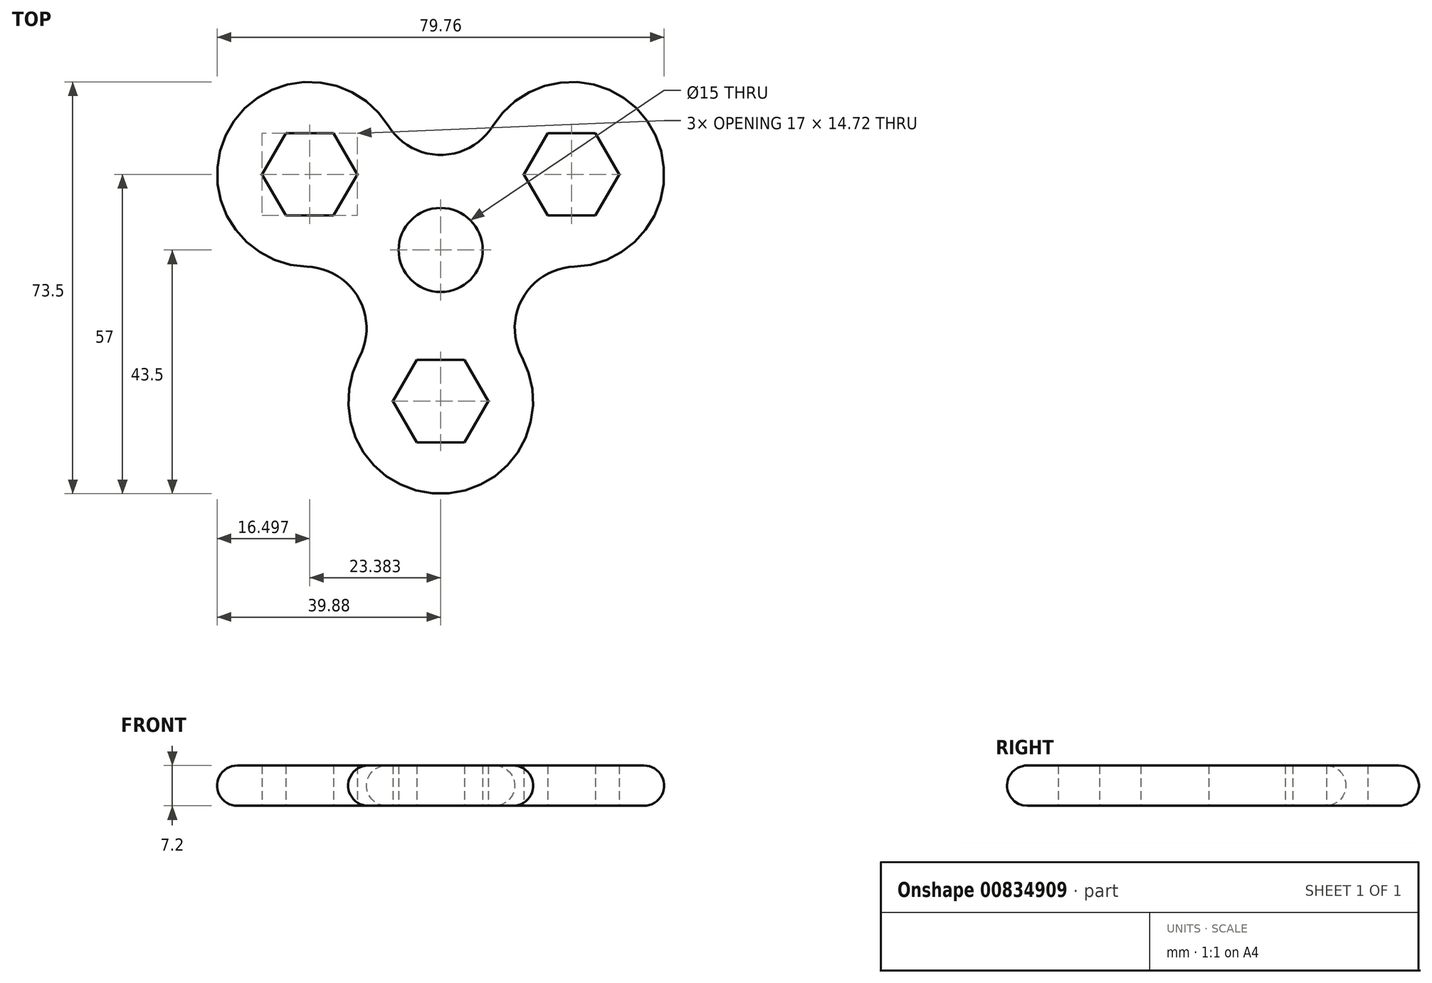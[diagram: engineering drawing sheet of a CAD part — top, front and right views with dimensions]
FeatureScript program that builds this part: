
annotation { "Feature Type Name" : "Feature", "Feature Type Description" : "" }
export const myFeature = defineFeature(function(context is Context, id is Id, definition is map)
    precondition{}
    {
        {
            var Q0;
            Q0=qCreatedBy(makeId("Top.planeOp"),FACE);
            var sketch = newSketch(context, id + "F0", { "sketchPlane" : qUnion([Q0])});
            skLineSegment(sketch, "E0", {"start": v(0, 0) * mm, "end": v(0, -27) * mm, "construction": true});
            skArc(sketch, "E1", {"start": v(-14.54, -19.2) * mm, "mid": v(0, -43.5) * mm, "end": v(14.54, -19.2) * mm});
            skLineSegment(sketch, "E2", {"start": v(-34.97, -27) * mm, "end": v(30.88, -27) * mm, "construction": true});
            skArc(sketch, "E3", {"start": v(23.89, -3) * mm, "mid": v(14.7, -8.49) * mm, "end": v(14.54, -19.2) * mm});
            skArc(sketch, "E4.1.0", {"start": v(-9.35, 22.18) * mm, "mid": v(-37.67, 21.75) * mm, "end": v(-23.89, -3) * mm});
            skArc(sketch, "E4.1.1", {"start": v(-14.54, -19.2) * mm, "mid": v(-14.7, -8.49) * mm, "end": v(-23.89, -3) * mm});
            skArc(sketch, "E4.2.0", {"start": v(23.89, -3) * mm, "mid": v(37.67, 21.75) * mm, "end": v(9.35, 22.18) * mm});
            skArc(sketch, "E4.2.1", {"start": v(-9.35, 22.18) * mm, "mid": v(0, 16.97) * mm, "end": v(9.35, 22.18) * mm});
            skPoint(sketch, "E4.center", {"position": v(0, 0) * mm});
            skLineSegment(sketch, "E4.anchor2", {"start": v(0, 0) * mm, "end": v(23.38, 13.5) * mm, "construction": true});
            skCircle(sketch, "E5", {"center": v(0, 0) * mm, "radius": 7.5 * mm});
            skCircle(sketch, "E6.cCircle", {"center": v(0, -27) * mm, "radius": 7.36 * mm, "construction": true});
            skLineSegment(sketch, "E6.0", {"start": v(4.25, -34.36) * mm, "end": v(-4.25, -34.36) * mm});
            skLineSegment(sketch, "E6.1", {"start": v(-4.25, -34.36) * mm, "end": v(-8.5, -27) * mm});
            skLineSegment(sketch, "E6.2", {"start": v(-8.5, -27) * mm, "end": v(-4.25, -19.64) * mm});
            skLineSegment(sketch, "E6.3", {"start": v(-4.25, -19.64) * mm, "end": v(4.25, -19.64) * mm});
            skLineSegment(sketch, "E6.4", {"start": v(4.25, -19.64) * mm, "end": v(8.5, -27) * mm});
            skLineSegment(sketch, "E6.5", {"start": v(8.5, -27) * mm, "end": v(4.25, -34.36) * mm});
            skPoint(sketch, "E6.0.midPoint", {"position": v(0, -34.36) * mm});
            skLineSegment(sketch, "E7.1.0", {"start": v(19.13, 6.14) * mm, "end": v(14.88, 13.5) * mm});
            skLineSegment(sketch, "E7.1.1", {"start": v(14.88, 13.5) * mm, "end": v(19.13, 20.86) * mm});
            skLineSegment(sketch, "E7.1.2", {"start": v(19.13, 20.86) * mm, "end": v(27.63, 20.86) * mm});
            skLineSegment(sketch, "E7.1.3", {"start": v(27.63, 20.86) * mm, "end": v(31.88, 13.5) * mm});
            skLineSegment(sketch, "E7.1.4", {"start": v(31.88, 13.5) * mm, "end": v(27.63, 6.14) * mm});
            skLineSegment(sketch, "E7.1.5", {"start": v(27.63, 6.14) * mm, "end": v(19.13, 6.14) * mm});
            skLineSegment(sketch, "E7.2.0", {"start": v(-14.88, 13.5) * mm, "end": v(-19.13, 6.14) * mm});
            skLineSegment(sketch, "E7.2.1", {"start": v(-19.13, 6.14) * mm, "end": v(-27.63, 6.14) * mm});
            skLineSegment(sketch, "E7.2.2", {"start": v(-27.63, 6.14) * mm, "end": v(-31.88, 13.5) * mm});
            skLineSegment(sketch, "E7.2.3", {"start": v(-31.88, 13.5) * mm, "end": v(-27.63, 20.86) * mm});
            skLineSegment(sketch, "E7.2.4", {"start": v(-27.63, 20.86) * mm, "end": v(-19.13, 20.86) * mm});
            skLineSegment(sketch, "E7.2.5", {"start": v(-19.13, 20.86) * mm, "end": v(-14.88, 13.5) * mm});
            skSolve(sketch);
        }
        {
            var Q0;
            {var subQ3=sQuery(id+"F0.wireOp",EDGE,"E3");Q0=makeQuery(id+"F0.imprint","IMPRINT",FACE,{"disambiguationData":[TD([[makeQuery(id+"F0.imprint","IMPRINT",EDGE,{"derivedFrom":subQ3}),-1.0]])]});}
            var Q1;
            Q1=makeQuery(id+"F0.imprint","IMPRINT",FACE,{"disambiguationData":[TD([[makeQuery(id+"F0.imprint","IMPRINT",EDGE,{"derivedFrom":sQuery(id+"F0.wireOp",EDGE,"cb8a32ce-8ee4-4620-8715-a1c9f472d884.2.0")}),-1.0]])]});
            var Q2;
            Q2=makeQuery(id+"F0.imprint","IMPRINT",FACE,{"disambiguationData":[TD([[makeQuery(id+"F0.imprint","IMPRINT",EDGE,{"derivedFrom":sQuery(id+"F0.wireOp",EDGE,"cb8a32ce-8ee4-4620-8715-a1c9f472d884.1.0")}),-1.0]])]});
            var Q3;
            Q3=makeQuery(id+"F0.imprint","IMPRINT",FACE,{"disambiguationData":[TD([[makeQuery(id+"F0.imprint","IMPRINT",EDGE,{"derivedFrom":sQuery(id+"F0.wireOp",EDGE,"KCJkTyUw-eKYJ-XEc1-Kacx-7hHiqveRcXMb")}),-1.0]])]});
            extrude(context, id + "F1", {"entities" : qUnion([Q0, Q1, Q2, Q3]), "depth" : 7.2 * mm, "offsetDistance" : 25 * mm});
        }
        {
            var Q0;
            Q0=makeQuery(id+"F1.opExtrude","CAP_EDGE",EDGE,{"disambiguationData":[OSD([sQuery(id+"F0.wireOp",EDGE,"E3")])],"isStart":false});
            var Q1;
            Q1=makeQuery(id+"F1.opExtrude","CAP_EDGE",EDGE,{"disambiguationData":[OSD([sQuery(id+"F0.wireOp",EDGE,"E3")])],"isStart":true});
            fillet(context, id + "F2", {"entities" : qUnion([Q0, Q1]), "radius" : 3.6 * mm, "tangentPropagation" : true, "allowEdgeOverflow" : false});
        }
    });
